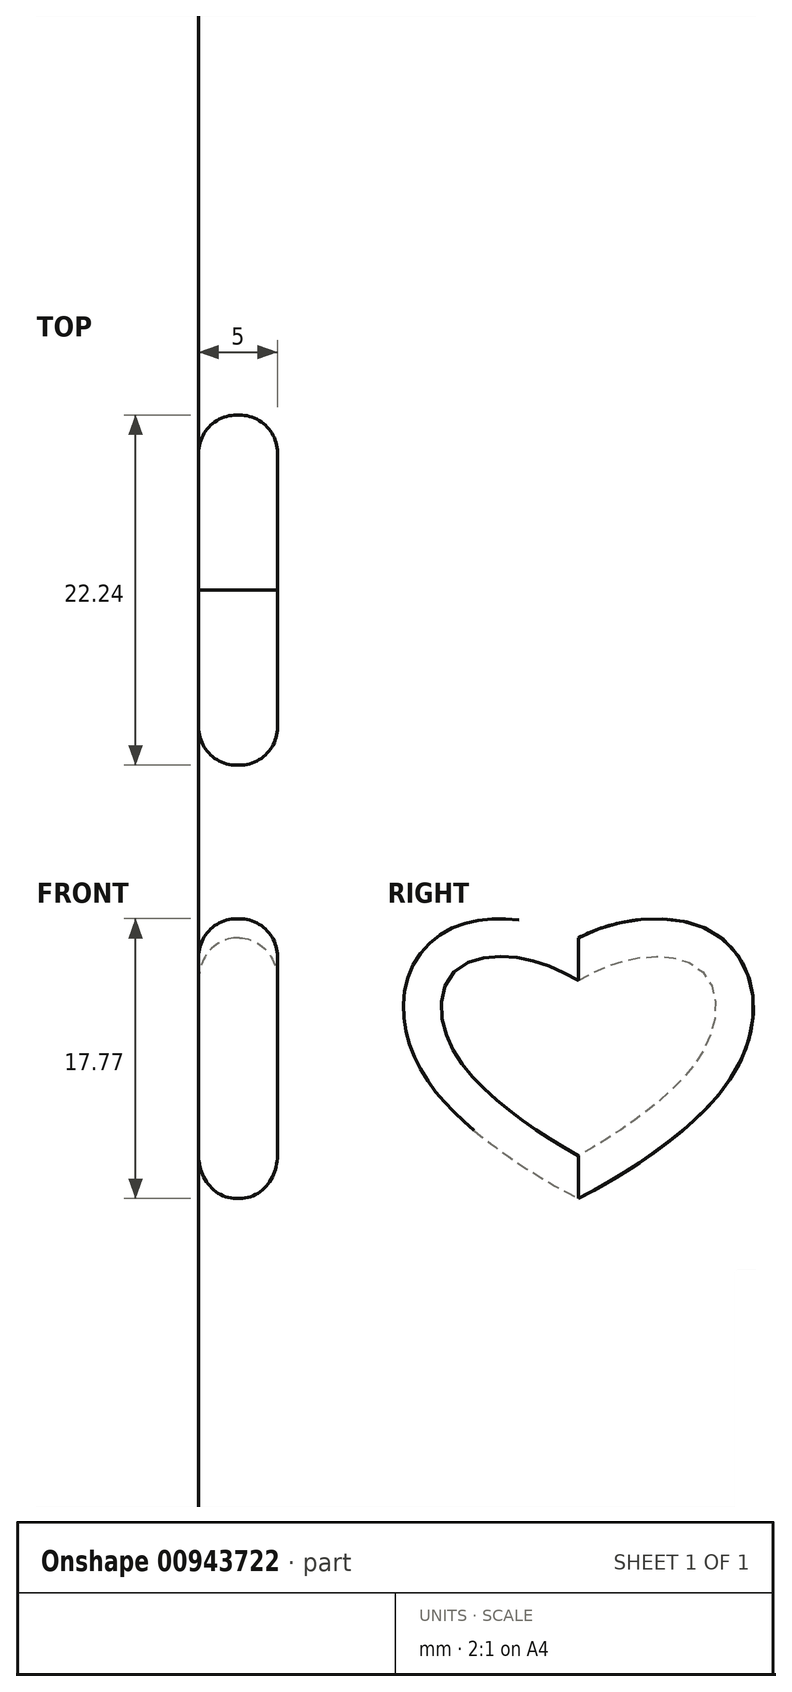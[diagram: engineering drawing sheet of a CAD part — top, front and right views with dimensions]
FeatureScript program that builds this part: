
annotation { "Feature Type Name" : "Feature", "Feature Type Description" : "" }
export const myFeature = defineFeature(function(context is Context, id is Id, definition is map)
    precondition{}
    {
        {
            var Q0;
            Q0=qCreatedBy(makeId("Front.planeOp"),FACE);
            var sketch = newSketch(context, id + "F0", { "sketchPlane" : qUnion([Q0])});
            skPoint(sketch, "E0.0.internal.orphan", {"position": v(0, 44.96) * mm});
            skPoint(sketch, "E0.4.internal.orphan", {"position": v(0, -26.4) * mm});
            skPoint(sketch, "E1.1.internal.orphan", {"position": v(23.35, 44.96) * mm});
            skFitSpline(sketch, "E2", {"points": [v(0, 23.1) * mm, v(18.14, 29.37) * mm, v(32.81, 24.42) * mm, v(33.96, 10.99) * mm, v(0, -26.4) * mm], "startDerivative": vector(77.59, 38.72) * mm, "endDerivative": vector(-119.16, -108.04) * mm});
            skLineSegment(sketch, "E3", {"start": v(1.3, -25.23) * mm, "end": v(1.35, -26.93) * mm, "construction": true});
            skLineSegment(sketch, "E4", {"start": v(0, 23.1) * mm, "end": v(0, -26.4) * mm});
            skFitSpline(sketch, "E5.MirrorCS", {"points": [v(0, 23.1) * mm, v(-18.14, 29.37) * mm, v(-32.81, 24.42) * mm, v(-33.96, 10.99) * mm, v(0, -26.4) * mm], "startDerivative": vector(-77.59, 38.72) * mm, "endDerivative": vector(119.16, -108.04) * mm});
            skSolve(sketch);
        }
        {
            var Q0;
            Q0=makeQuery(id+"F0.imprint","IMPRINT",FACE,{"disambiguationData":[TD([[makeQuery(id+"F0.imprint","IMPRINT",EDGE,{"derivedFrom":sQuery(id+"F0.wireOp",EDGE,"E2")}),-1.0]])]});
            var Q1;
            Q1=makeQuery(id+"F0.imprint","IMPRINT",FACE,{"disambiguationData":[TD([[makeQuery(id+"F0.imprint","IMPRINT",EDGE,{"derivedFrom":sQuery(id+"F0.wireOp",EDGE,"E4")}),-1.0]])]});
            var Q2;
            Q2=sQuery(id+"F0.wireOp",EDGE,"E2");
            var Q3;
            Q3=sQuery(id+"F0.wireOp",EDGE,"E4");
            revolve(context, id + "F1", {"bodyType" : ToolBodyType.SURFACE, "surfaceOperationType" : NewSurfaceOperationType.NEW, "entities" : qUnion([Q0, Q1]), "surfaceEntities" : qUnion([Q2]), "axis" : qUnion([Q3]), "revolveType" : RevolveType.TWO_DIRECTIONS, "angle" : 30 * degree, "angleBack" : 330 * degree});
        }
        {
            var Q0;
            Q0=qCreatedBy(makeId("Front.planeOp"),FACE);
            var sketch = newSketch(context, id + "F2", { "sketchPlane" : qUnion([Q0])});
            skLineSegment(sketch, "E6", {"start": v(0, 22.75) * mm, "end": v(0, -26.23) * mm, "construction": true});
            skSolve(sketch);
        }
        {
            var Q0;
            Q0=makeQuery(id+"F1.opRevolve","SWEPT_BODY",BODY,{"disambiguationData":[OSD([sQuery(id+"F0.wireOp",EDGE,"E2")])]});
            var Q1;
            Q1=sQuery(id+"F2.wireOp",EDGE,"E6");
            circularPattern(context, id + "F3", {"entities" : qUnion([Q0]), "axis" : qUnion([Q1]), "angle" : 360 * degree, "instanceCount" : 3, "equalSpace" : true});
        }
        {
            var Q0;
            Q0=qCreatedBy(makeId("Right.planeOp"),FACE);
            var sketch = newSketch(context, id + "F4", { "sketchPlane" : qUnion([Q0])});
            skFitSpline(sketch, "E7", {"points": [v(0, 23.2) * mm, v(-7.59, 24) * mm, v(-10.95, 20.26) * mm, v(-8.84, 13.16) * mm, v(0, 6.66) * mm], "startDerivative": vector(-28.36, 14.9) * mm, "endDerivative": vector(19.09, -9.55) * mm});
            skLineSegment(sketch, "E8", {"start": v(0, 23.2) * mm, "end": v(0, 6.66) * mm, "construction": true});
            skFitSpline(sketch, "E9.MirrorCS", {"points": [v(0, 23.2) * mm, v(7.59, 24) * mm, v(10.95, 20.26) * mm, v(8.84, 13.16) * mm, v(0, 6.66) * mm], "startDerivative": vector(28.36, 14.9) * mm, "endDerivative": vector(-19.09, -9.55) * mm});
            skSolve(sketch);
        }
        {
            var Q0;
            Q0=makeQuery(id+"F4.imprint","IMPRINT",FACE,{"disambiguationData":[TD([[makeQuery(id+"F4.imprint","IMPRINT",EDGE,{"derivedFrom":sQuery(id+"F4.wireOp",EDGE,"E7")}),1.0]])]});
            extrude(context, id + "F5", {"entities" : qUnion([Q0]), "endBound" : BoundingType.SYMMETRIC, "depth" : 5 * mm, "offsetDistance" : 25.4 * mm});
        }
        {
            var Q0;
            Q0=makeQuery(id+"F5.opExtrude","CAP_EDGE",EDGE,{"disambiguationData":[OSD([sQuery(id+"F4.wireOp",EDGE,"E9.MirrorCS")])],"isStart":true});
            var Q1;
            Q1=makeQuery(id+"F5.opExtrude","CAP_EDGE",EDGE,{"disambiguationData":[OSD([sQuery(id+"F4.wireOp",EDGE,"E7")])],"isStart":true});
            fillet(context, id + "F6", {"entities" : qUnion([Q0, Q1]), "radius" : 2.4 * mm, "tangentPropagation" : true, "allowEdgeOverflow" : false});
        }
        {
            var Q0;
            Q0=makeQuery(id+"F5.opExtrude","CAP_EDGE",EDGE,{"disambiguationData":[OSD([sQuery(id+"F4.wireOp",EDGE,"E7")])],"isStart":false});
            var Q1;
            Q1=makeQuery(id+"F5.opExtrude","CAP_EDGE",EDGE,{"disambiguationData":[OSD([sQuery(id+"F4.wireOp",EDGE,"E9.MirrorCS")])],"isStart":false});
            fillet(context, id + "F7", {"entities" : qUnion([Q0, Q1]), "radius" : 2.4 * mm, "tangentPropagation" : true, "allowEdgeOverflow" : false});
        }
    });
